# Revit family: D2LED
name_source: partatom
category: Lighting Fixtures
units: mm (PartAtom-declared; Revit-internal decimal feet)

## family parameters
Cut with Voids When Loaded = No
Host = Face
Light Source = Yes
OmniClass Number = 23.80.70.11
OmniClass Title = Luminaries for Internal Lighting
Part Type = Normal
Room Calculation Point = No
Round Connector Dimension = Use Diameter
Shared = No

## types (1)
- D2LED-2D9LED12L30K8FL35
    Apparent Load = 0 VA
    Backbox = Aluminium
    Color Filter = 16777215
    Default Elevation = 48.000"
    Description = 2 inch LED Downlight Open & Wall Wash
    Dimming Lamp Color Temperature Shift = <None>
    Fixture Retention Spring = Black
    Heat Sink = Black
    Insulation sensor = Black
    J-TUBE = Aluminium
    Lamp = LED
    Manufacturer = Prescolite
    Model = D2LED
    Photometric Web File = D2LED-2D9LED12L30K8FL35.IES
    Reflector = reflector
    Tilt Angle = -90.00°
    URL = https://www.currentlighting.com
    Wattage Comments = 22W
    Wire = Wire Finish

## geometry (parser evidence)
native form markers: Blend x3, Sweep x1
no freeform markers — native parametric forms only
